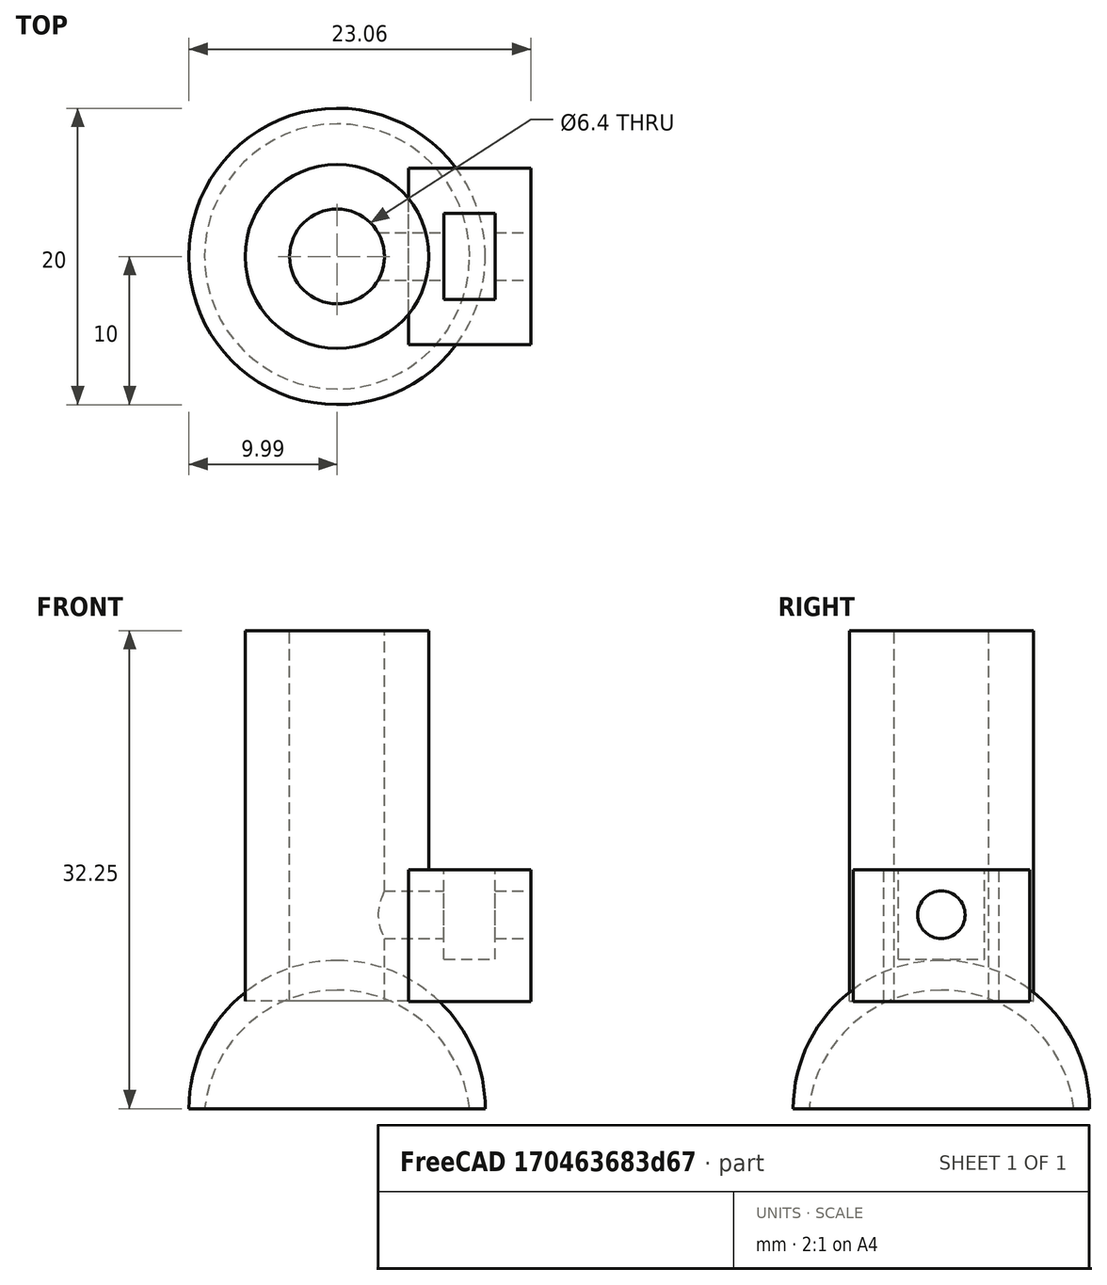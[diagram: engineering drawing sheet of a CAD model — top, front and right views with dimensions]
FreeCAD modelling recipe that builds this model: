
FCSTD DOCUMENT  (FreeCAD 0.21R33771 (Git))
Label: motor_clutch
License: All rights reserved
LicenseURL: http://en.wikipedia.org/wiki/All_rights_reserved
objects: Part::Cylinder×3, Part::Cut×3, Part::Box×2, Part::Fuse×2, Part::Sphere×2, Part::Compound×2, Part::Feature×1
note: 15 computed .brp shape members not serialized (recipe doc carries the construction recipe); baked Part::Feature solids carry a one-line shape summary decoded from their .brp

FEATURE [Part::Box] cube002
  AttacherType = Attacher::AttachEngine3D
  Height = 8.91
  Length = 8.25
  Placement = pos=(-4.125,-5.955,-6.455) rot=(0,0,1;0rad)
  Width = 11.91
FEATURE [Part::Cylinder] cylinder003
  Angle = 360
  AttacherType = Attacher::AttachEngine3D
  FirstAngle = 0
  Height = 50
  Placement = pos=(0,0,-1) rot=(0,0,1;0rad)
  Radius = 3.2
  SecondAngle = 0
FEATURE [Part::Cylinder] cylinder004
  Angle = 360
  AttacherType = Attacher::AttachEngine3D
  FirstAngle = 0
  Height = 25
  Radius = 6.2
  SecondAngle = 0
FEATURE [Part::Box] cube003
  AttacherType = Attacher::AttachEngine3D
  Height = 11.11
  Length = 3.45
  Placement = pos=(-1.725,-2.9,-3.6) rot=(0,0,1;0rad)
  Width = 5.8
FEATURE [Part::Cylinder] cylinder005
  Angle = 360
  AttacherType = Attacher::AttachEngine3D
  FirstAngle = 0
  Height = 22.9
  Placement = pos=(0,0,5.83) rot=(0,1,0;1.5708rad)
  Radius = 1.6
  SecondAngle = 0
FEATURE [Part::Cut] difference002
  Base = -> cube002
  Placement = pos=(8.95,0,6.425) rot=(0,0,1;0rad)
  Tool = -> cube003
FEATURE [Part::Fuse] union002
  Base = -> cylinder003
  Tool = -> cylinder005
FEATURE [Part::Fuse] union003
  Base = -> cylinder004
  Tool = -> difference002
FEATURE [Part::Cut] difference003  label="wheel_fit_holder"
  Base = -> union003
  Tool = -> union002
FEATURE [Part::Sphere] Sphere
  Angle1 = -90
  Angle2 = 0
  Angle3 = 360
  AttacherType = Attacher::AttachEngine3D
  Placement = pos=(16.5428,-16.9323,-1e-16) rot=(0,0,1;0rad)
  Radius = 10
FEATURE [Part::Sphere] Sphere001
  Angle1 = -90
  Angle2 = 0
  Angle3 = 360
  AttacherType = Attacher::AttachEngine3D
  Placement = pos=(16.5428,-16.9323,1) rot=(0,0,1;0rad)
  Radius = 9
FEATURE [Part::Cut] Cut006
  Base = -> Sphere
  Placement = pos=(-0.04745,0.430952,1) rot=(0,0,1;0rad)
  Tool = -> Sphere001
FEATURE [Part::Feature] Base002
  shape: bbox 32.96 x 33 x 8 mm, 664 faces, 0 solids (baked)
FEATURE [Part::Compound] Compound001
  Links = -> [Cut006,Base002]
  Placement = pos=(-16.49,-16.5,-6.25) rot=(1,0,0;3.14159rad)
FEATURE [Part::Compound] Compound002  label="wheel_assembly"
  Links = -> [difference003,Compound001]
  Placement = pos=(-24,-21,14) rot=(0,0,1;0rad)
